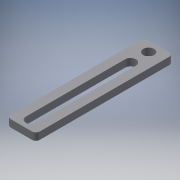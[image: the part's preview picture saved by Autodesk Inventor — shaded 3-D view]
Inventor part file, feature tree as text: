
AUTODESK INVENTOR PART (.ipt)
format: ipt  version: 2018 (Build 220112000, 112)  size: 128,512 bytes
history: native  units: mm
features: reference x7, other x6, extrude x1, fillet x1, sketch x1
ambient origin geometry x8: Origin, YZ Plane, XZ Plane, XY Plane, X Axis, Y Axis, Z Axis, Center Point
bodies: Solid1 (feature_tree)
feature tree (16):
  extrude  "Extrusion1"  Depth=8.0mm
  fillet  "Fillet1"  Radius=3.5mm
  sketch  "Sketch1"  dims[d0=4.0mm d1=8.0mm d2=3.5mm d3=5.0mm d5=2.0mm d6=0.0mm d7=1.0mm d8=2.75mm d9=3.5mm]
  reference  "Reference1"
  reference  "Reference2"
  reference  "Reference3"
  reference  "Reference4"
  reference  "Reference5"
  reference  "Reference6"
  reference  "Reference7"
  other  "<userpath>\OneDrive\Documents\Inventor\TSA\2018\Animatronics\Tortoise\Turtle3.iam"
  other  "Turtle3.iam"
  other  "ButtonMountCarrier:1"
  other  "ButtonMount:1"
  other  "ButtonMountLegs:1"
  other  "ButtonMountLegs:2"
